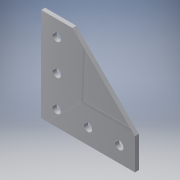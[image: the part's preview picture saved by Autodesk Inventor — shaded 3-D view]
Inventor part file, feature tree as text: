
AUTODESK INVENTOR PART (.ipt)
format: ipt  version: 2016 (Build 200138000, 138)  size: 111,104 bytes
history: native  units: in
note: dims shown in document units (in); Inventor stores cm internally (conversion verified against a paired STEP export)
features: extrude x1, sketch x1
ambient origin geometry x8: Origin, YZ Plane, XZ Plane, XY Plane, X Axis, Y Axis, Z Axis, Center Point
bodies: Solid1 (feature_tree)
feature tree (2):
  extrude  "Extrusion1"  Depth=0.125in
  sketch  "Sketch1"  dims[d0=3.0in d1=1.0in d2=1.0in d3=3.0in d6=0.2656in d10=1.5in d11=2.5in d12=1.5in d15=0.5in d16=0.5in d17=2.5in d18=0.125in d19=0.0in]
